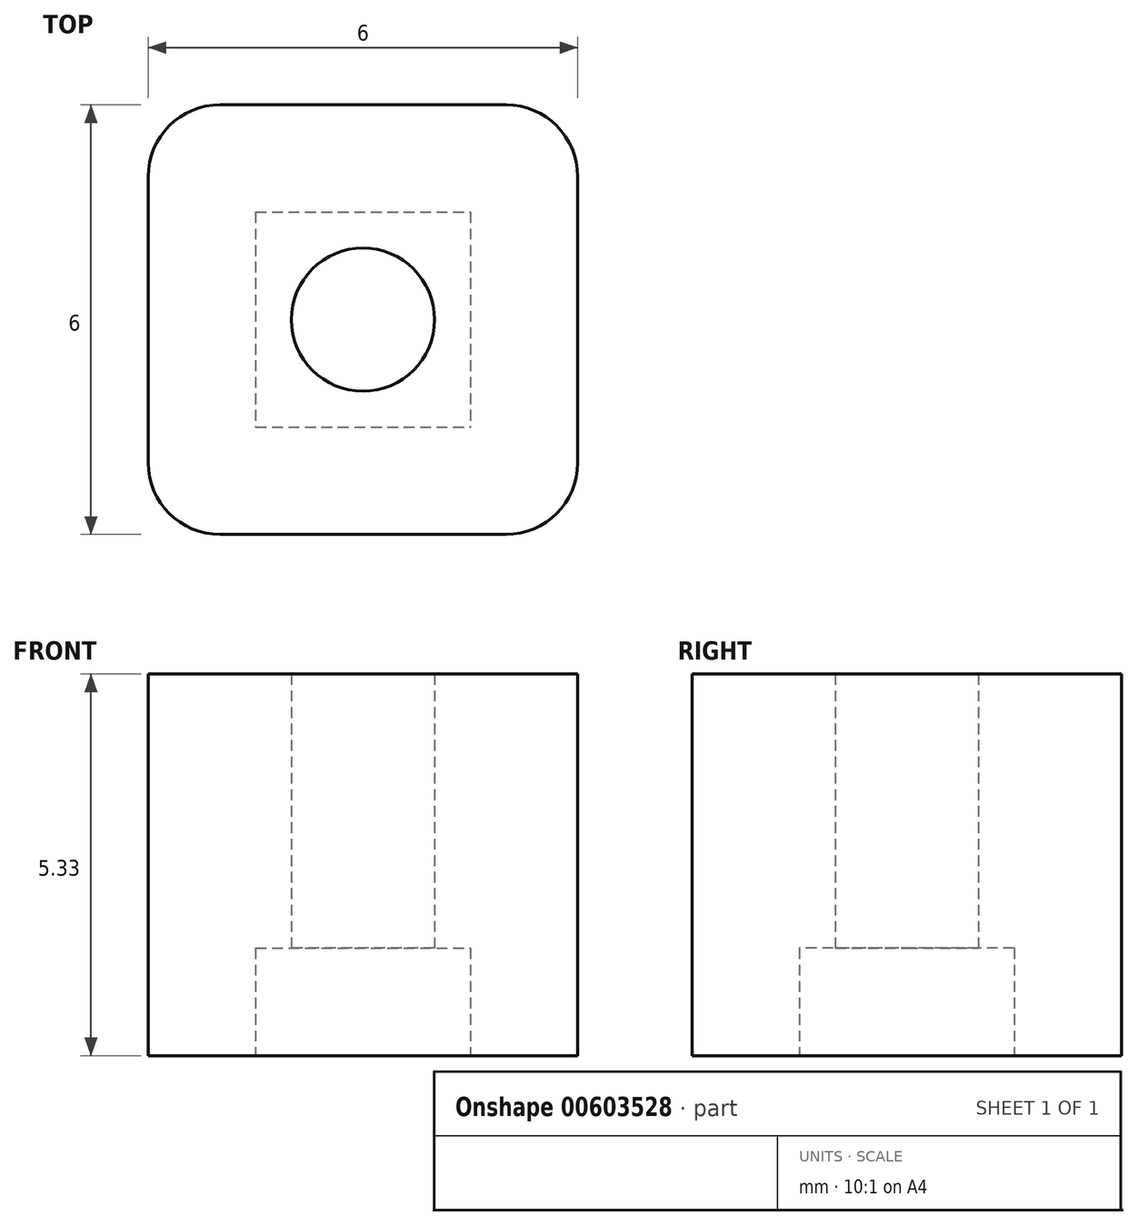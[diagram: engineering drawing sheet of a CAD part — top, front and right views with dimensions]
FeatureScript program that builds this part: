
annotation { "Feature Type Name" : "Feature", "Feature Type Description" : "" }
export const myFeature = defineFeature(function(context is Context, id is Id, definition is map)
    precondition{}
    {
        {
            var Q0;
            Q0=qCreatedBy(makeId("Top.planeOp"),FACE);
            var sketch = newSketch(context, id + "F0", { "sketchPlane" : qUnion([Q0])});
            skLineSegment(sketch, "E0.bottom", {"start": v(3, 3) * mm, "end": v(-3, 3) * mm});
            skLineSegment(sketch, "E0.top", {"start": v(3, -3) * mm, "end": v(-3, -3) * mm});
            skLineSegment(sketch, "E0.left", {"start": v(3, 3) * mm, "end": v(3, -3) * mm});
            skLineSegment(sketch, "E0.right", {"start": v(-3, 3) * mm, "end": v(-3, -3) * mm});
            skPoint(sketch, "E0.middle", {"position": v(0, 0) * mm});
            skLineSegment(sketch, "E1.bottom", {"start": v(-1.5, 1.5) * mm, "end": v(1.5, 1.5) * mm});
            skLineSegment(sketch, "E1.top", {"start": v(-1.5, -1.5) * mm, "end": v(1.5, -1.5) * mm});
            skLineSegment(sketch, "E1.left", {"start": v(-1.5, 1.5) * mm, "end": v(-1.5, -1.5) * mm});
            skLineSegment(sketch, "E1.right", {"start": v(1.5, 1.5) * mm, "end": v(1.5, -1.5) * mm});
            skCircle(sketch, "E2", {"center": v(0, 0) * mm, "radius": 1 * mm});
            skSolve(sketch);
        }
        {
            var Q0;
            Q0=qCreatedBy(makeId("Front.planeOp"),FACE);
            var sketch = newSketch(context, id + "F1", { "sketchPlane" : qUnion([Q0])});
            skLineSegment(sketch, "E3.bottom", {"start": v(1, 0) * mm, "end": v(-1, 0) * mm});
            skLineSegment(sketch, "E3.top", {"start": v(1, 0.5) * mm, "end": v(-1, 0.5) * mm});
            skLineSegment(sketch, "E3.left", {"start": v(1, 0) * mm, "end": v(1, 0.5) * mm});
            skLineSegment(sketch, "E3.right", {"start": v(-1, 0) * mm, "end": v(-1, 0.5) * mm});
            skPoint(sketch, "E3.middle", {"position": v(0, 0.25) * mm});
            skLineSegment(sketch, "E4.bottom", {"start": v(-1, 0.5) * mm, "end": v(1, 0.5) * mm});
            skLineSegment(sketch, "E4.top", {"start": v(-1, 5.33) * mm, "end": v(1, 5.33) * mm});
            skLineSegment(sketch, "E4.left", {"start": v(-1, 0.5) * mm, "end": v(-1, 5.33) * mm});
            skLineSegment(sketch, "E4.right", {"start": v(1, 0.5) * mm, "end": v(1, 5.33) * mm});
            skLineSegment(sketch, "E5", {"start": v(-1, 5.33) * mm, "end": v(1, 0.5) * mm});
            skLineSegment(sketch, "E6", {"start": v(1, 5.33) * mm, "end": v(-1, 0.5) * mm});
            skSolve(sketch);
        }
        {
            var Q0;
            Q0=makeQuery(id+"F0.imprint","IMPRINT",FACE,{"disambiguationData":[TD([[makeQuery(id+"F0.imprint","IMPRINT",EDGE,{"derivedFrom":sQuery(id+"F0.wireOp",EDGE,"E0.bottom")}),1.0]])]});
            var Q1;
            Q1=makeQuery(id+"F0.imprint","IMPRINT",FACE,{"disambiguationData":[TD([[makeQuery(id+"F0.imprint","IMPRINT",EDGE,{"derivedFrom":sQuery(id+"F0.wireOp",EDGE,"E1.bottom")}),-1.0]])]});
            var Q2;
            Q2=sQuery(id+"F1.wireOp",VERTEX,"E4.top.start");
            extrude(context, id + "F2", {"entities" : qUnion([Q0, Q1]), "endBound" : BoundingType.UP_TO_VERTEX, "depth" : 25 * mm, "endBoundEntityVertex" : qUnion([Q2]), "offsetDistance" : 25 * mm});
        }
        {
            var Q0;
            Q0=makeQuery(id+"F0.imprint","IMPRINT",FACE,{"disambiguationData":[TD([[makeQuery(id+"F0.imprint","IMPRINT",EDGE,{"derivedFrom":sQuery(id+"F0.wireOp",EDGE,"E1.bottom")}),-1.0]])]});
            extrude(context, id + "F3", {"entities" : qUnion([Q0]), "operationType" : NewBodyOperationType.REMOVE, "depth" : 1.5 * mm, "offsetDistance" : 25 * mm});
        }
        {
            var Q0;
            Q0=makeQuery(id+"F2.opExtrude","SWEPT_EDGE",EDGE,{"disambiguationData":[OSD([sQuery(id+"F0.wireOp",EDGE,"E0.top"),sQuery(id+"F0.wireOp",EDGE,"E0.right")])]});
            var Q1;
            Q1=makeQuery(id+"F2.opExtrude","SWEPT_EDGE",EDGE,{"disambiguationData":[OSD([sQuery(id+"F0.wireOp",EDGE,"E0.top"),sQuery(id+"F0.wireOp",EDGE,"E0.left")])]});
            var Q2;
            Q2=makeQuery(id+"F2.opExtrude","SWEPT_EDGE",EDGE,{"disambiguationData":[OSD([sQuery(id+"F0.wireOp",EDGE,"E0.bottom"),sQuery(id+"F0.wireOp",EDGE,"E0.left")])]});
            var Q3;
            Q3=makeQuery(id+"F2.opExtrude","SWEPT_EDGE",EDGE,{"disambiguationData":[OSD([sQuery(id+"F0.wireOp",EDGE,"E0.bottom"),sQuery(id+"F0.wireOp",EDGE,"E0.right")])]});
            fillet(context, id + "F4", {"entities" : qUnion([Q0, Q1, Q2, Q3]), "radius" : 1 * mm, "tangentPropagation" : true, "allowEdgeOverflow" : false});
        }
    });
